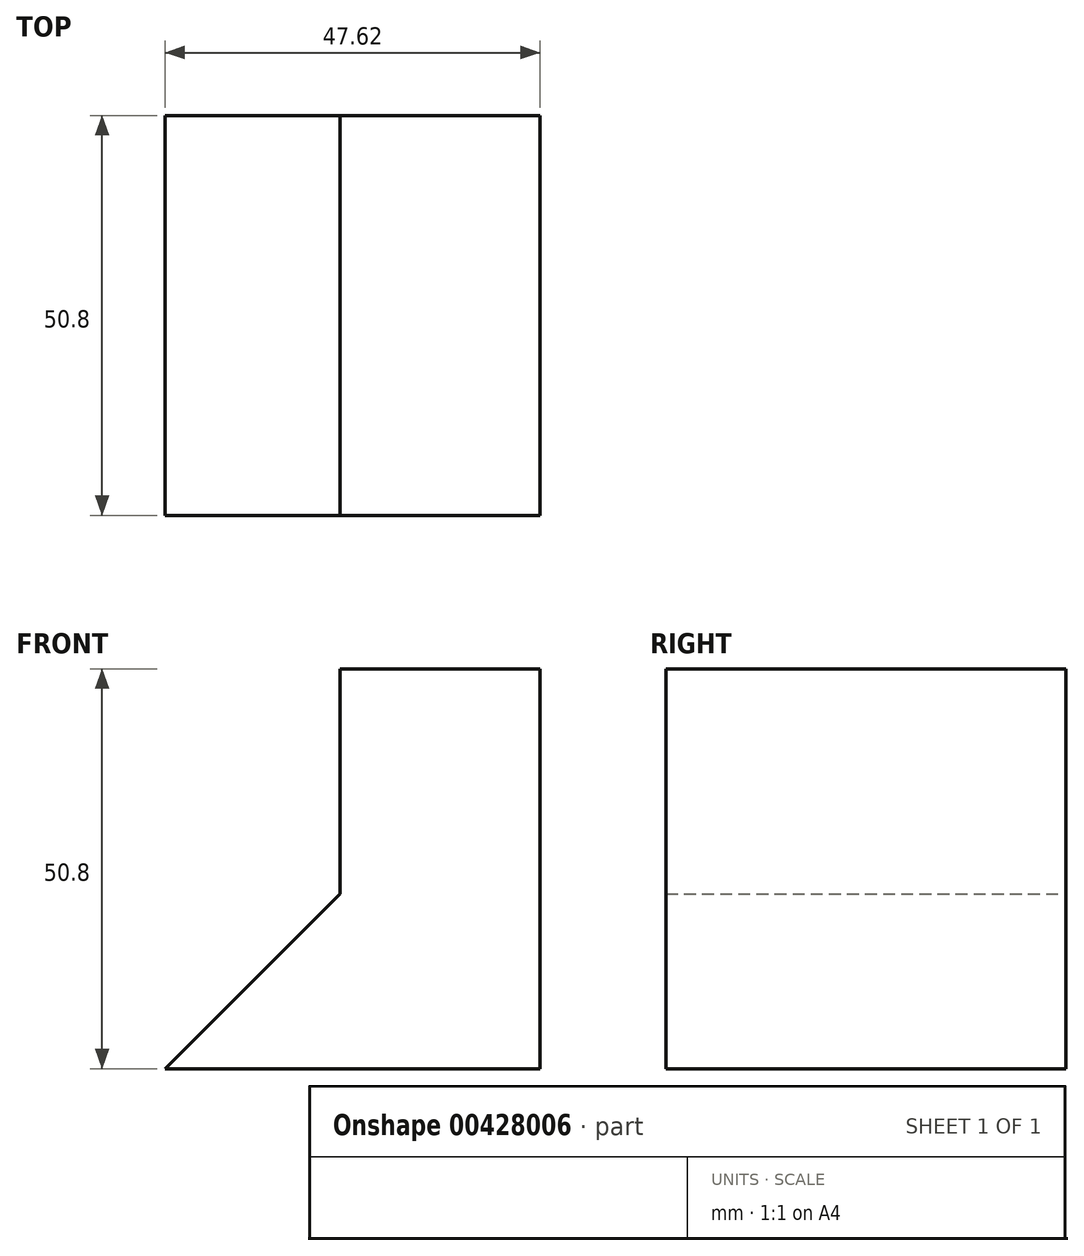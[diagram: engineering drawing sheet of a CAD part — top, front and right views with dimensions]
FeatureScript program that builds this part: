
annotation { "Feature Type Name" : "Feature", "Feature Type Description" : "" }
export const myFeature = defineFeature(function(context is Context, id is Id, definition is map)
    precondition{}
    {
        {
            var Q0;
            Q0=qCreatedBy(makeId("Front.planeOp"),FACE);
            var sketch = newSketch(context, id + "F0", { "sketchPlane" : qUnion([Q0])});
            skLineSegment(sketch, "E0.bottom", {"start": v(0, 0) * mm, "end": v(-25.4, 0) * mm});
            skLineSegment(sketch, "E0.top", {"start": v(0, 50.8) * mm, "end": v(-25.4, 50.8) * mm});
            skLineSegment(sketch, "E0.left", {"start": v(0, 0) * mm, "end": v(0, 50.8) * mm});
            skLineSegment(sketch, "E1", {"start": v(-25.4, 50.8) * mm, "end": v(-25.4, 0) * mm});
            skPoint(sketch, "E0.right.end.orphan", {"position": v(-50.8, 50.8) * mm});
            skSolve(sketch);
        }
        {
            var Q0;
            Q0 = qSketchRegion(id + "F0", true);
            extrude(context, id + "F1", {"entities" : qUnion([Q0]), "depth" : 50.8 * mm});
        }
        {
            var Q0;
            Q0=qCreatedBy(makeId("Front.planeOp"),FACE);
            var sketch = newSketch(context, id + "F2", { "sketchPlane" : qUnion([Q0])});
            skLineSegment(sketch, "E2.bottom", {"start": v(-22.22, 0) * mm, "end": v(-47.62, 0) * mm});
            skLineSegment(sketch, "E2.left", {"start": v(-22.22, 0) * mm, "end": v(-22.22, 25.4) * mm});
            skLineSegment(sketch, "E3", {"start": v(-22.22, 25.4) * mm, "end": v(-47.62, 0) * mm});
            skLineSegment(sketch, "E4", {"start": v(-111.27, 77.53) * mm, "end": v(-112.96, 79.22) * mm});
            skSolve(sketch);
        }
        {
            var Q0;
            Q0 = qSketchRegion(id + "F2", true);
            extrude(context, id + "F3", {"entities" : qUnion([Q0]), "operationType" : NewBodyOperationType.ADD, "depth" : 50.8 * mm});
        }
    });
